# Revit family: VETRO TOP FIX
name_source: partatom
category: Generic Models
units: mm (PartAtom-declared; Revit-internal decimal feet)

## family parameters
Always vertical = Yes
Can host rebar = No
Cut with Voids When Loaded = No
Part Type = Normal
Room Calculation Point = No
Round Connector Dimension = Use Diameter
Shared = No
Work Plane-Based = No

## types (7) — shared parameters
HAND RAIL HEIGHT = 950 mm  [stored 3.1168 ft]
Hand Rail Height = 950 mm  [stored 3.1168 ft]
MAX POST SPACING = 1000 mm  [stored 3.28084 ft]
Manufacturer = UNEX SYSTEMS
URL = WWW.UNEX.CO.NZ
zero-valued in all types: Default Elevation

## per-type parameters (varying)
| type | ART TOP RAIL | Description | HAND RAIL ON / OFF | HEIGHT | Keynote | LENGTH | LLR (Round hand rail) | Model | PPR TOP RAIL | Pannel QTY | Post Height | Post QTY | VRE TOP RAIL | VRR TOP RAIL | VRT TOP RAIL |
| VETRO WITH VRE | No | UNEX VETRO SEMI-FRAMELESS GLASS WITH NO RAIL | Yes | 1100 mm  [stored 3.60892 ft] | UNEX, VETRO TOP FIX (NO RAIL) | 2500 mm  [stored 8.2021 ft] | No | UNEX VETRO SEMI-FRAMELESS GLASS WITH NO RAIL | No | 3 | 1084 mm  [stored 3.55643 ft] | 4 | Yes | No | No |
| VETRO WITH PRR | No | UNEX VETRO SEMI-FRAMELESS GLASS WITH PRR TOP RAIL | Yes | 1100 mm  [stored 3.60892 ft] | UNEX SYSTEMS, VETRO TOP FIX BALUSTRADE | 2500 mm  [stored 8.2021 ft] | No | UNEX, VETRO TOP FIX (PRR) | Yes | 3 | 1084 mm  [stored 3.55643 ft] | 4 | No | No | No |
| VETRO WITH ART | Yes | UNEX VETRO SEMI-FRAMELESS GLASS WITH ART TOP RAIL | Yes | 1100 mm  [stored 3.60892 ft] | UNEX SYSTEMS, VETRO TOP FIX BALUSTRADE | 2500 mm  [stored 8.2021 ft] | No | UNEX, VETRO TOP FIX (ART) | No | 3 | 1084 mm  [stored 3.55643 ft] | 4 | No | No | No |
| VETRO WITH VRT | No | UNEX VETRO SEMI-FRAMELESS GLASS WITH VRT TOP RAIL | Yes | 1100 mm  [stored 3.60892 ft] | UNEX SYSTEMS, VETRO TOP FIX BALUSTRADE | 2500 mm  [stored 8.2021 ft] | No | UNEX, VETRO TOP FIX (VRT) | No | 3 | 1084 mm  [stored 3.55643 ft] | 4 | No | No | Yes |
| VETRO WITH VRR | No | UNEX VETRO SEMI-FRAMELESS GLASS WITH VRR TOP RAIL | Yes | 1100 mm  [stored 3.60892 ft] | UNEX SYSTEMS, VETRO TOP FIX BALUSTRADE | 2500 mm  [stored 8.2021 ft] | No | UNEX, VETRO TOP FIX (VRR) | No | 3 | 1084 mm  [stored 3.55643 ft] | 4 | No | Yes | No |
| VETRO WITH LLR | No | UNEX VETRO SEMI-FRAMELESS GLASS WITH LLR  RAIL | Yes | 1400 mm | UNEX SYSTEMS, VETRO TOP FIX BALUSTRADE | 3485 mm | Yes | UNEX, VETRO TOP FIX (LRR) | No | 3 | 1384 mm | 4 | No | No | No |
| VETRO (NO HAND RAIL) | No | UNEX VETRO SEMI-FRAMELESS GLASS WITH NO RAIL | No | 1500 mm  [stored 4.92126 ft] | UNEX, VETRO TOP FIX (NO RAIL) | 3541 mm | No | UNEX VETRO SEMI-FRAMELESS GLASS WITH NO RAIL | No | 4 | 1484 mm | 5 | No | No | No |

note: [stored X ft] marks values corroborated as IEEE doubles in the binary element streams (Revit-internal decimal feet)

## geometry (parser evidence)
native form markers: Blend x2, Sweep x32
no freeform markers — native parametric forms only
